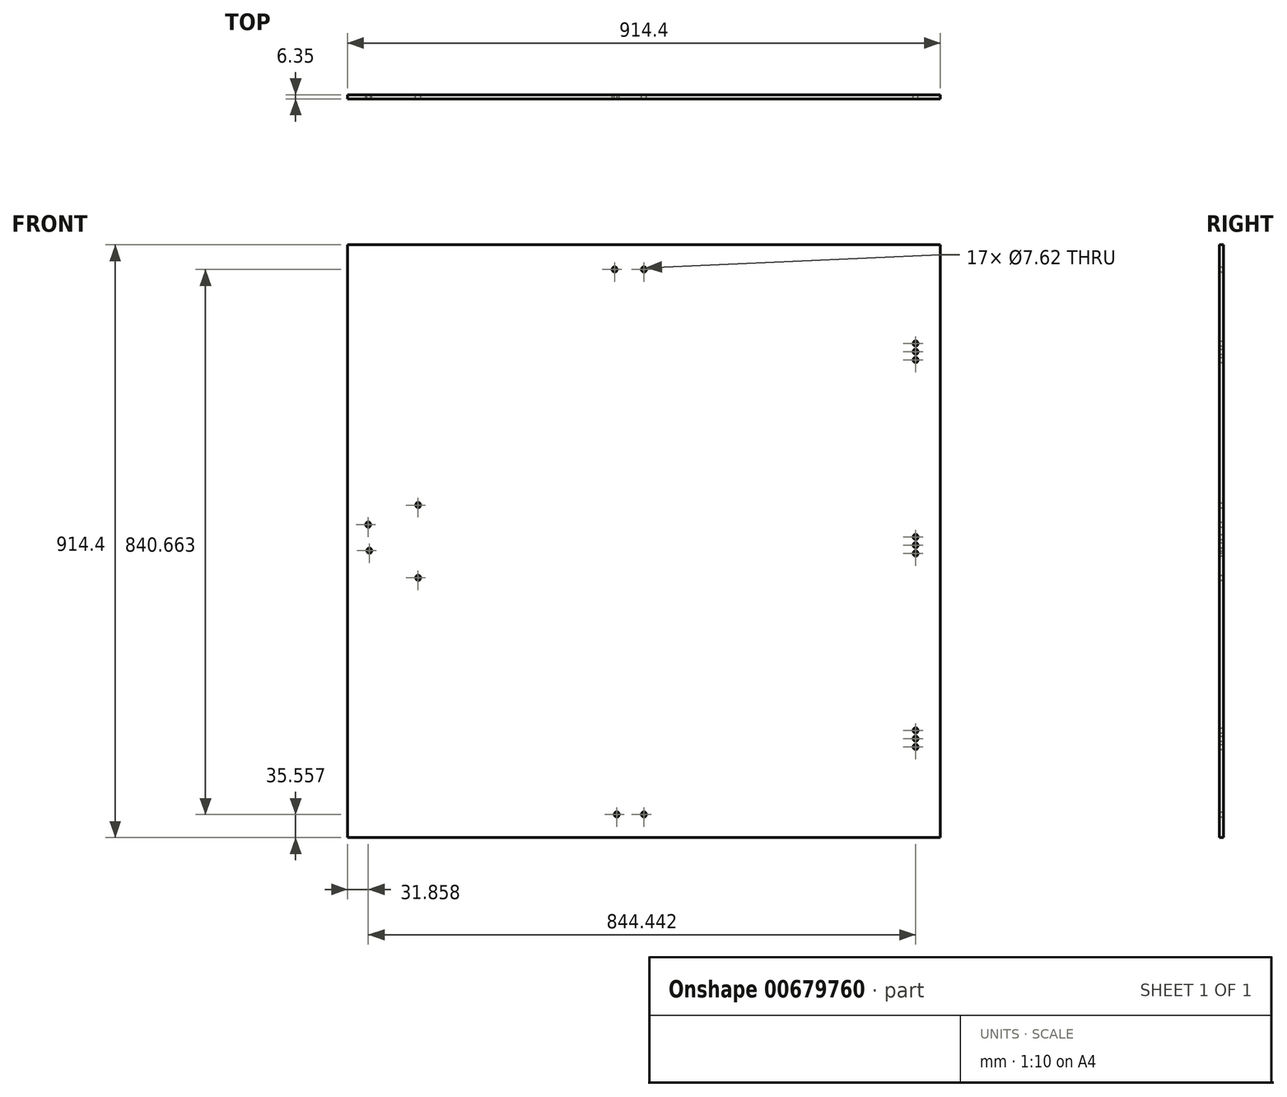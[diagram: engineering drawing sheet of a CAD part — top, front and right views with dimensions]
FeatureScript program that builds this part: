
annotation { "Feature Type Name" : "Feature", "Feature Type Description" : "" }
export const myFeature = defineFeature(function(context is Context, id is Id, definition is map)
    precondition{}
    {
        {
            var Q0;
            Q0=qCreatedBy(makeId("Front.planeOp"),FACE);
            var sketch = newSketch(context, id + "F0", { "sketchPlane" : qUnion([Q0])});
            skLineSegment(sketch, "E0.bottom", {"start": v(457.2, 457.2) * mm, "end": v(-457.2, 457.2) * mm});
            skLineSegment(sketch, "E0.top", {"start": v(457.2, -457.2) * mm, "end": v(-457.2, -457.2) * mm});
            skLineSegment(sketch, "E0.left", {"start": v(457.2, 457.2) * mm, "end": v(457.2, -457.2) * mm});
            skLineSegment(sketch, "E0.right", {"start": v(-457.2, 457.2) * mm, "end": v(-457.2, -457.2) * mm});
            skPoint(sketch, "E0.middle", {"position": v(0, 0) * mm});
            skLineSegment(sketch, "E1", {"start": v(419.1, 495.94) * mm, "end": v(419.1, -483.24) * mm});
            skPoint(sketch, "E2", {"position": v(419.1, 292.1) * mm});
            skPoint(sketch, "E3", {"position": v(419.1, 304.8) * mm});
            skPoint(sketch, "E4", {"position": v(419.1, 279.4) * mm});
            skPoint(sketch, "E5", {"position": v(419.1, -6.35) * mm});
            skPoint(sketch, "E6", {"position": v(419.1, 6.35) * mm});
            skPoint(sketch, "E7", {"position": v(419.1, -19.05) * mm});
            skPoint(sketch, "E8", {"position": v(419.1, -292.1) * mm});
            skPoint(sketch, "E9", {"position": v(419.1, -304.8) * mm});
            skPoint(sketch, "E10", {"position": v(419.1, -317.5) * mm});
            skPoint(sketch, "E11", {"position": v(-45.2, 419.02) * mm});
            skPoint(sketch, "E12", {"position": v(0, 419.02) * mm});
            skPoint(sketch, "E13", {"position": v(-425.34, 25.48) * mm});
            skPoint(sketch, "E14", {"position": v(-423.67, -14.7) * mm});
            skPoint(sketch, "E15", {"position": v(-41.85, -421.64) * mm});
            skPoint(sketch, "E16", {"position": v(-348.3, 55.63) * mm});
            skPoint(sketch, "E17", {"position": v(-348.3, -56.57) * mm});
            skPoint(sketch, "E18", {"position": v(0, -421.64) * mm});
            skSolve(sketch);
        }
        {
            var Q0;
            Q0=makeQuery(id+"F0.imprint","IMPRINT",FACE,{"disambiguationData":[TD([[makeQuery(id+"F0.imprint","IMPRINT",EDGE,{"derivedFrom":sQuery(id+"F0.wireOp",EDGE,"E0.bottom")}),1.0]])]});
            var Q1;
            {var subQ0=sQuery(id+"F0.wireOp",EDGE,"0D6Oxsa1-KB6H-3I89-oIXq-XYD1ljEdMzyG");var subQ1=sQuery(id+"F0.wireOp",EDGE,"E0.left");var subQ2=makeQuery(id+"F0.imprint","INTERSECT",VERTEX,{"derivedFrom":[subQ1,subQ0]});Q1=makeQuery(id+"F0.imprint","IMPRINT",FACE,{"disambiguationData":[TD([[makeQuery(id+"F0.imprint","IMPRINT",EDGE,{"disambiguationData":[TD([[subQ2,-1.0]])],"derivedFrom":subQ1}),-1.0]])]});}
            var Q2;
            {var subQ4=sQuery(id+"F0.wireOp",EDGE,"E0.right");Q2=makeQuery(id+"F0.imprint","IMPRINT",FACE,{"disambiguationData":[TD([[makeQuery(id+"F0.imprint","IMPRINT",EDGE,{"derivedFrom":subQ4}),1.0]])]});}
            var Q3;
            {var subQ0=sQuery(id+"F0.wireOp",EDGE,"vb2pCEtQ-5Jag-0zdW-JLCa-0zm3M6n4kmGi");var subQ1=sQuery(id+"F0.wireOp",EDGE,"E0.left");var subQ2=makeQuery(id+"F0.imprint","INTERSECT",VERTEX,{"derivedFrom":[subQ1,subQ0]});Q3=makeQuery(id+"F0.imprint","IMPRINT",FACE,{"disambiguationData":[TD([[makeQuery(id+"F0.imprint","IMPRINT",EDGE,{"disambiguationData":[TD([[subQ2,-1.0]])],"derivedFrom":subQ1}),-1.0]])]});}
            var Q4;
            {var subQ0=sQuery(id+"F0.wireOp",EDGE,"E0.left");var subQ1=sQuery(id+"F0.wireOp",EDGE,"E0.top");var subQ2=makeQuery(id+"F0.imprint","INTERSECT",VERTEX,{"derivedFrom":[subQ1,subQ0]});Q4=makeQuery(id+"F0.imprint","IMPRINT",FACE,{"disambiguationData":[TD([[makeQuery(id+"F0.imprint","IMPRINT",EDGE,{"disambiguationData":[TD([[subQ2,-1.0]])],"derivedFrom":subQ1}),-1.0]])]});}
            extrude(context, id + "F1", {"entities" : qUnion([Q0, Q1, Q2, Q3, Q4]), "depth" : 6.35 * mm, "offsetDistance" : 25.4 * mm});
        }
        {
            var Q0;
            Q0=sQuery(id+"F0.wireOp",VERTEX,"E3");
            var Q1;
            Q1=sQuery(id+"F0.wireOp",VERTEX,"E2");
            var Q2;
            Q2=sQuery(id+"F0.wireOp",VERTEX,"E4");
            var Q3;
            Q3=sQuery(id+"F0.wireOp",VERTEX,"E6");
            var Q4;
            Q4=sQuery(id+"F0.wireOp",VERTEX,"E7");
            var Q5;
            Q5=sQuery(id+"F0.wireOp",VERTEX,"E10");
            var Q6;
            Q6=sQuery(id+"F0.wireOp",VERTEX,"E9");
            var Q7;
            Q7=sQuery(id+"F0.wireOp",VERTEX,"E8");
            var Q8;
            Q8=sQuery(id+"F0.wireOp",VERTEX,"E5");
            var Q9;
            Q9=sQuery(id+"F0.wireOp",VERTEX,"E16");
            var Q10;
            Q10=sQuery(id+"F0.wireOp",VERTEX,"E17");
            var Q11;
            Q11=sQuery(id+"F0.wireOp",VERTEX,"E14");
            var Q12;
            Q12=sQuery(id+"F0.wireOp",VERTEX,"E13");
            var Q13;
            Q13=sQuery(id+"F0.wireOp",VERTEX,"E11");
            var Q14;
            Q14=sQuery(id+"F0.wireOp",VERTEX,"E12");
            var Q15;
            Q15=sQuery(id+"F0.wireOp",VERTEX,"E15");
            var Q16;
            Q16=sQuery(id+"F0.wireOp",VERTEX,"E18");
            var Q17;
            Q17=makeQuery(id+"F1.opExtrude","SWEPT_BODY",BODY,{"disambiguationData":[OSD([sQuery(id+"F0.wireOp",EDGE,"E0.bottom"),sQuery(id+"F0.wireOp",EDGE,"E0.top"),sQuery(id+"F0.wireOp",EDGE,"E0.left"),sQuery(id+"F0.wireOp",EDGE,"E0.right")])]});
            hole(context, id + "F2", {"style" : HoleStyle.C_SINK, "endStyle" : HoleEndStyle.THROUGH, "oppositeDirection" : true, "holeDiameter" : 7.62 * mm, "cSinkDiameter" : 9.52 * mm, "cSinkAngle" : 90 * degree, "majorDiameter" : 6.35 * mm, "isTappedThrough" : true, "tappedDepth" : 12.7 * mm, "tapClearance" : 3, "locations" : qUnion([Q0, Q1, Q2, Q3, Q4, Q5, Q6, Q7, Q8, Q9, Q10, Q11, Q12, Q13, Q14, Q15, Q16]), "scope" : qUnion([Q17])});
        }
    });
